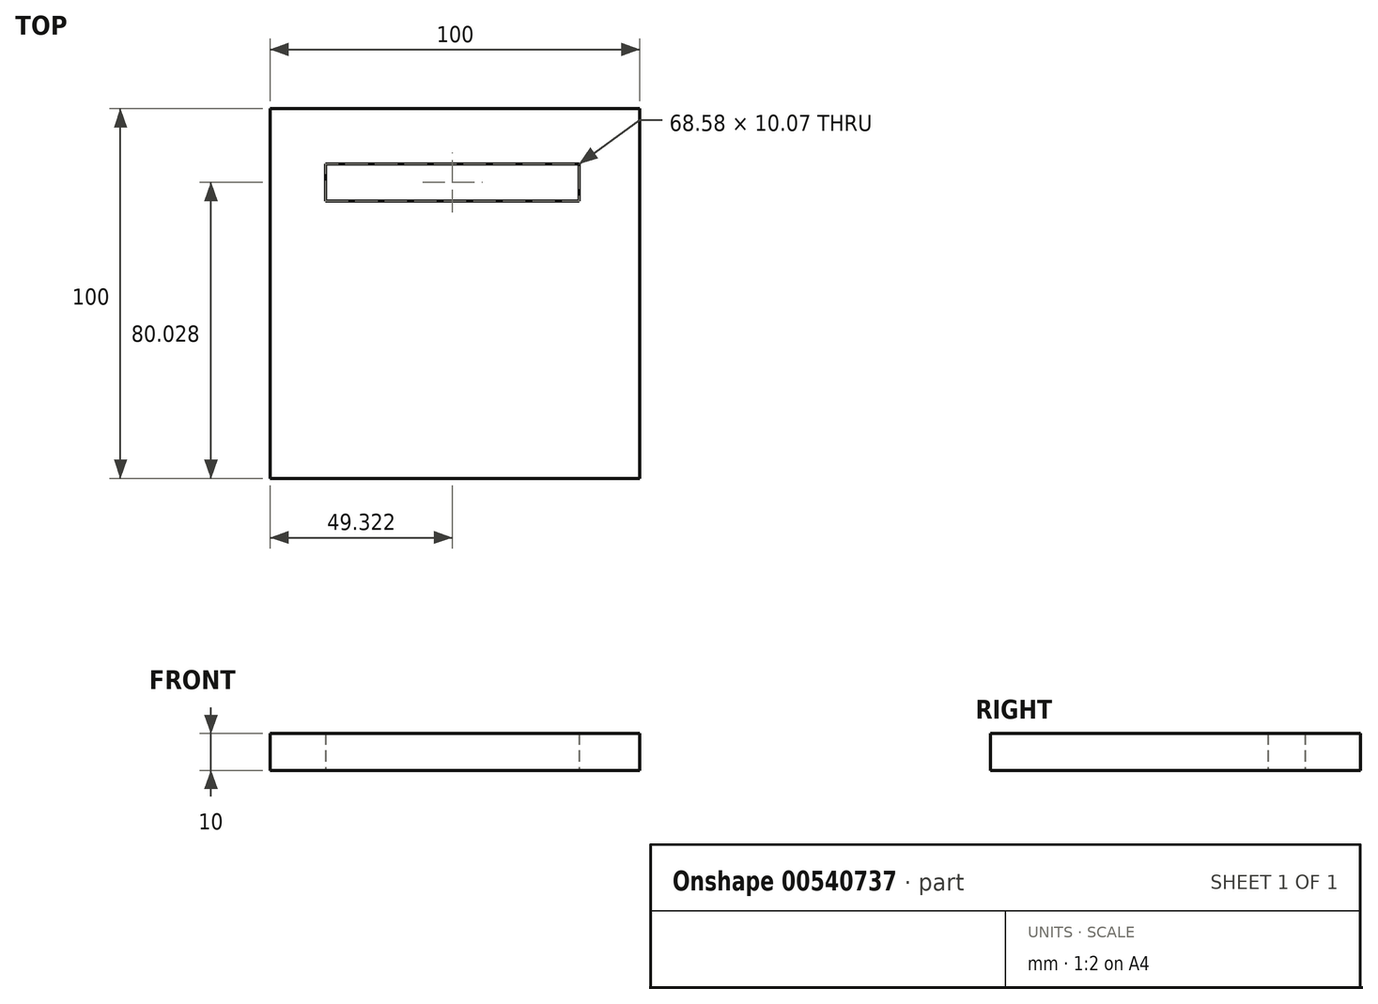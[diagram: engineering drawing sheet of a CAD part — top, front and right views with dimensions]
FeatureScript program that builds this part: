
annotation { "Feature Type Name" : "Feature", "Feature Type Description" : "" }
export const myFeature = defineFeature(function(context is Context, id is Id, definition is map)
    precondition{}
    {
        {
            var Q0;
            Q0=qCreatedBy(makeId("Top.planeOp"),FACE);
            var sketch = newSketch(context, id + "F0", { "sketchPlane" : qUnion([Q0])});
            skLineSegment(sketch, "E0.bottom", {"start": v(50, 50) * mm, "end": v(-50, 50) * mm});
            skLineSegment(sketch, "E0.top", {"start": v(50, -50) * mm, "end": v(-50, -50) * mm});
            skLineSegment(sketch, "E0.left", {"start": v(50, 50) * mm, "end": v(50, -50) * mm});
            skLineSegment(sketch, "E0.right", {"start": v(-50, 50) * mm, "end": v(-50, -50) * mm});
            skPoint(sketch, "E0.middle", {"position": v(0, 0) * mm});
            skSolve(sketch);
        }
        {
            var Q0;
            Q0=makeQuery(id+"F0.imprint","IMPRINT",FACE,{"disambiguationData":[TD([[makeQuery(id+"F0.imprint","IMPRINT",EDGE,{"derivedFrom":sQuery(id+"F0.wireOp",EDGE,"E0.bottom")}),1.0]])]});
            extrude(context, id + "F1", {"entities" : qUnion([Q0]), "endBound" : BoundingType.SYMMETRIC, "depth" : 10 * mm, "offsetDistance" : 25 * mm});
        }
        {
            var Q0;
            Q0=qCreatedBy(makeId("Top.planeOp"),FACE);
            var sketch = newSketch(context, id + "F2", { "sketchPlane" : qUnion([Q0])});
            skLineSegment(sketch, "E1.bottom", {"start": v(-34.97, 35.06) * mm, "end": v(33.61, 35.06) * mm});
            skLineSegment(sketch, "E1.top", {"start": v(-34.97, 25) * mm, "end": v(33.61, 25) * mm});
            skLineSegment(sketch, "E1.left", {"start": v(-34.97, 35.06) * mm, "end": v(-34.97, 25) * mm});
            skLineSegment(sketch, "E1.right", {"start": v(33.61, 35.06) * mm, "end": v(33.61, 25) * mm});
            skSolve(sketch);
        }
        {
            var Q0;
            Q0 = qSketchRegion(id + "F2", true);
            extrude(context, id + "F3", {"entities" : qUnion([Q0]), "operationType" : NewBodyOperationType.REMOVE, "endBound" : BoundingType.SYMMETRIC, "depth" : 25 * mm, "offsetDistance" : 25 * mm});
        }
    });
